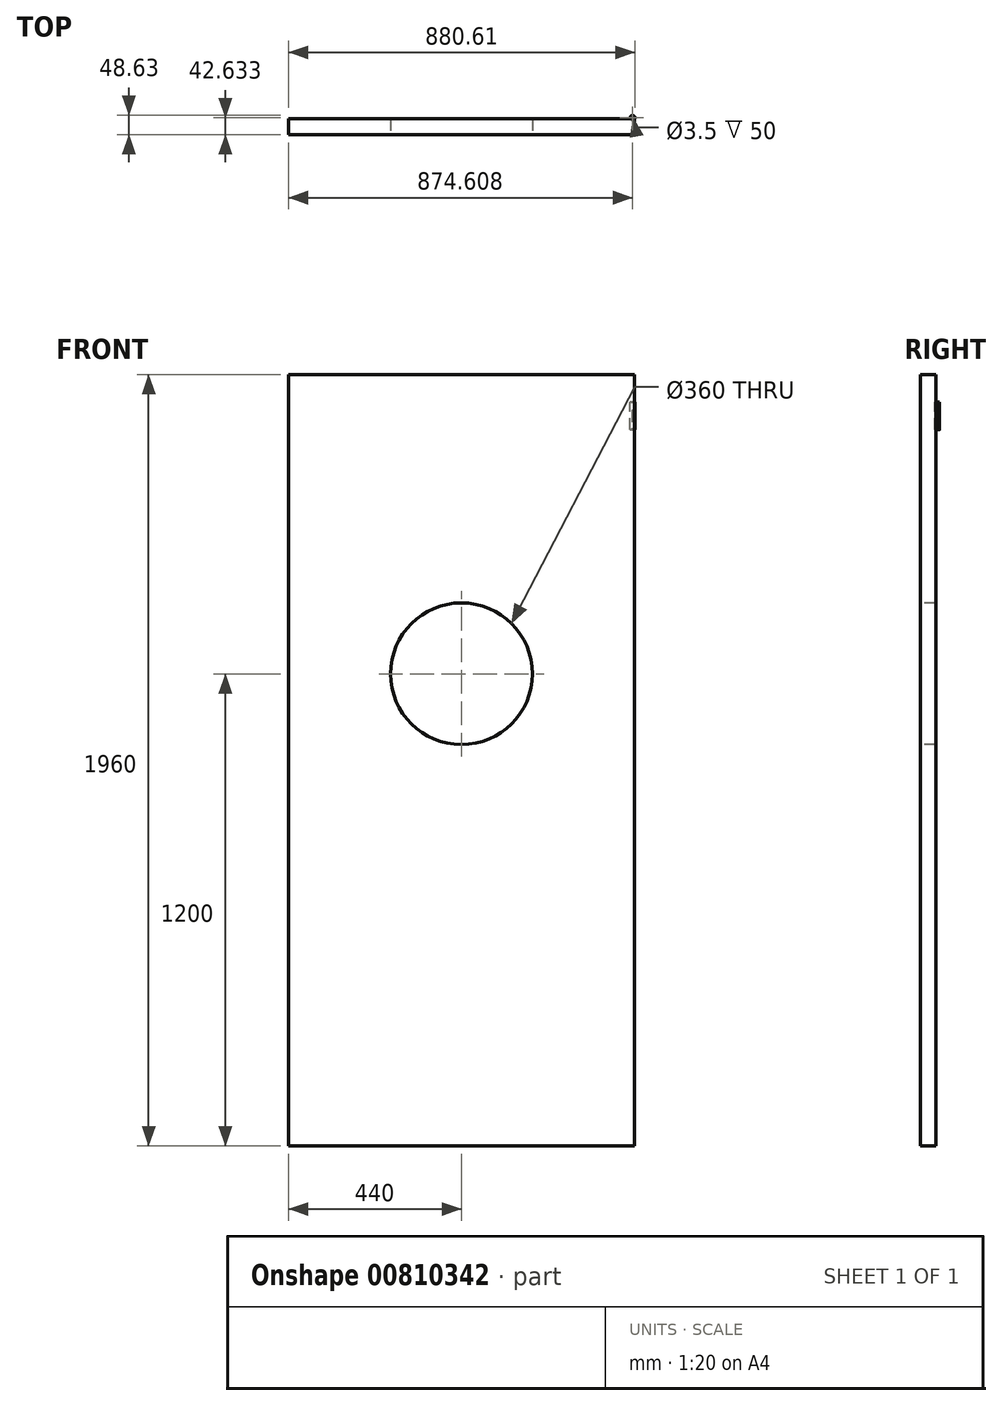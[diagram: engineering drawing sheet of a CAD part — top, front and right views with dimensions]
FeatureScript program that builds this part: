
annotation { "Feature Type Name" : "Feature", "Feature Type Description" : "" }
export const myFeature = defineFeature(function(context is Context, id is Id, definition is map)
    precondition{}
    {
        {
            var Q0;
            Q0=qCreatedBy(makeId("Front.planeOp"),FACE);
            var sketch = newSketch(context, id + "F0", { "sketchPlane" : qUnion([Q0])});
            skLineSegment(sketch, "E0.bottom", {"start": v(-440, 980) * mm, "end": v(440, 980) * mm});
            skLineSegment(sketch, "E0.top", {"start": v(-440, -980) * mm, "end": v(440, -980) * mm});
            skLineSegment(sketch, "E0.left", {"start": v(-440, 980) * mm, "end": v(-440, -980) * mm});
            skLineSegment(sketch, "E0.right", {"start": v(440, 980) * mm, "end": v(440, -980) * mm});
            skLineSegment(sketch, "E1", {"start": v(0, 1099.26) * mm, "end": v(0, -1203.47) * mm, "construction": true});
            skLineSegment(sketch, "E2", {"start": v(-880.9, 0) * mm, "end": v(1074.44, 0) * mm, "construction": true});
            skSolve(sketch);
        }
        {
            var Q0;
            Q0 = qSketchRegion(id + "F0", true);
            extrude(context, id + "F1", {"entities" : qUnion([Q0]), "depth" : 40 * mm, "offsetDistance" : 25.4 * mm});
        }
        {
            var Q0;
            Q0=makeQuery(id+"F1.opExtrude","CAP_FACE",FACE,{"disambiguationData":[OSD([sQuery(id+"F0.wireOp",EDGE,"E0.bottom"),sQuery(id+"F0.wireOp",EDGE,"E0.top"),sQuery(id+"F0.wireOp",EDGE,"E0.left"),sQuery(id+"F0.wireOp",EDGE,"E0.right")])],"isStart":false});
            var sketch = newSketch(context, id + "F2", { "sketchPlane" : qUnion([Q0])});
            skCircle(sketch, "E3", {"center": v(0, 220) * mm, "radius": 180 * mm});
            skSolve(sketch);
        }
        {
            var Q0;
            Q0 = qSketchRegion(id + "F2", true);
            extrude(context, id + "F3", {"entities" : qUnion([Q0]), "operationType" : NewBodyOperationType.REMOVE, "oppositeDirection" : true, "depth" : 116.84 * mm, "offsetDistance" : 25.4 * mm});
        }
        {
            var Q0;
            Q0=makeQuery(id+"F1.opExtrude","SWEPT_FACE",FACE,{"disambiguationData":[OSD([sQuery(id+"F0.wireOp",EDGE,"E0.bottom")])]});
            cPlane(context, id + "F4", {"entities" : qUnion([Q0]), "cplaneType" : CPlaneType.OFFSET, "offset" : 70 * mm, "oppositeDirection" : true, "width" : 152.4 * mm, "height" : 152.4 * mm});
        }
        {
            var Q0;
            Q0=qCreatedBy(id+"F4.planeOp",FACE);
            var sketch = newSketch(context, id + "F5", { "sketchPlane" : qUnion([Q0])});
            skCircle(sketch, "E4", {"center": v(434.6, 2.63) * mm, "radius": 6 * mm});
            skSolve(sketch);
        }
        {
            var Q0;
            Q0 = qSketchRegion(id + "F5", true);
            extrude(context, id + "F6", {"entities" : qUnion([Q0]), "oppositeDirection" : true, "depth" : 70 * mm, "offsetDistance" : 25.4 * mm});
        }
        {
            var Q0;
            Q0=makeQuery(id+"F6.opExtrude","CAP_FACE",FACE,{"disambiguationData":[OSD([sQuery(id+"F5.wireOp",EDGE,"E4")])],"isStart":false});
            var sketch = newSketch(context, id + "F7", { "sketchPlane" : qUnion([Q0])});
            skCircle(sketch, "E5", {"center": v(434.6, -2.63) * mm, "radius": 1.75 * mm});
            skSolve(sketch);
        }
        {
            var Q0;
            Q0 = qSketchRegion(id + "F7", true);
            extrude(context, id + "F8", {"entities" : qUnion([Q0]), "operationType" : NewBodyOperationType.REMOVE, "oppositeDirection" : true, "depth" : 50 * mm, "offsetDistance" : 25.4 * mm});
        }
    });
